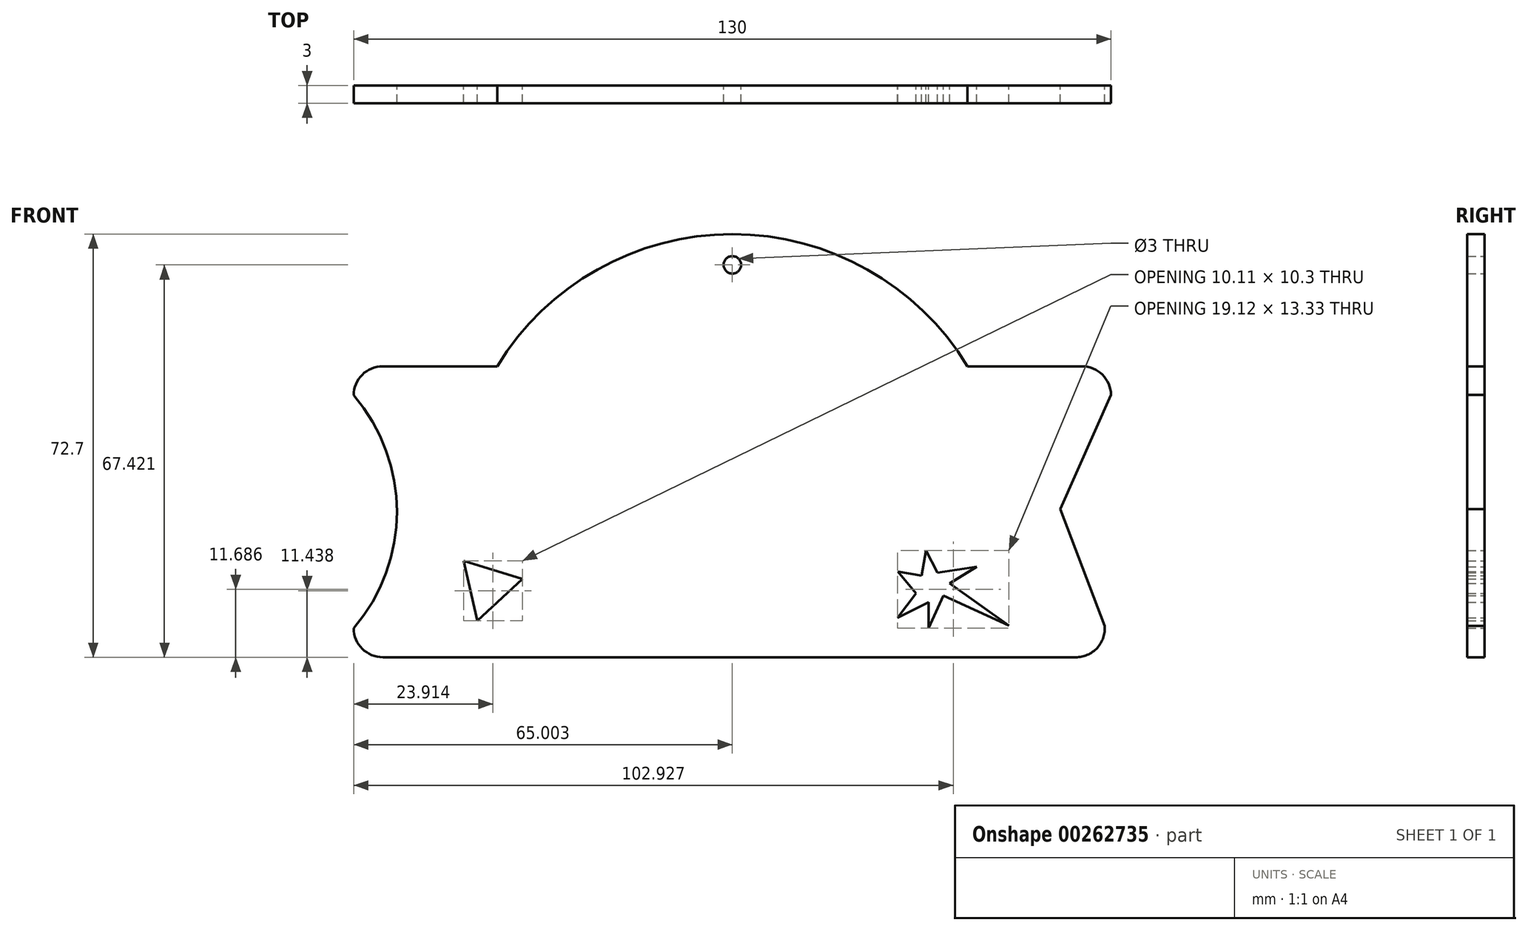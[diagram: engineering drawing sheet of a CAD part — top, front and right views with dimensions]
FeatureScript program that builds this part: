
annotation { "Feature Type Name" : "Feature", "Feature Type Description" : "" }
export const myFeature = defineFeature(function(context is Context, id is Id, definition is map)
    precondition{}
    {
        {
            var Q0;
            Q0=qCreatedBy(makeId("Front.planeOp"),FACE);
            var sketch = newSketch(context, id + "F0", { "sketchPlane" : qUnion([Q0])});
            skLineSegment(sketch, "E0.bottom", {"start": v(-100.37, 0) * mm, "end": v(18.58, 0) * mm});
            skLineSegment(sketch, "E0.top", {"start": v(-100.37, 50) * mm, "end": v(19.63, 50) * mm});
            skPoint(sketch, "E1", {"position": v(-40.37, 50) * mm});
            skPoint(sketch, "E2", {"position": v(15.96, 25.45) * mm});
            skArc(sketch, "E3", {"start": v(0, 50) * mm, "mid": v(-40.37, 72.7) * mm, "end": v(-80.73, 50) * mm});
            skCircle(sketch, "E4", {"center": v(-40.37, 67.42) * mm, "radius": 1.5 * mm});
            skPoint(sketch, "E5", {"position": v(-40.37, 39.6) * mm});
            skPoint(sketch, "E6", {"position": v(-105.37, 25) * mm});
            skPoint(sketch, "E7", {"position": v(-40.37, 0) * mm});
            skPoint(sketch, "E8", {"position": v(95.57, 25) * mm});
            skPoint(sketch, "E9.visualSharp", {"position": v(-105.37, 50) * mm});
            skArc(sketch, "E9.filletArc", {"start": v(-100.37, 50) * mm, "mid": v(-103.9, 48.54) * mm, "end": v(-105.37, 45) * mm});
            skPoint(sketch, "E10.visualSharp", {"position": v(-105.37, 0) * mm});
            skArc(sketch, "E10.filletArc", {"start": v(-105.37, 5) * mm, "mid": v(-103.9, 1.46) * mm, "end": v(-100.37, 0) * mm});
            skPoint(sketch, "E11.visualSharp", {"position": v(24.63, 0) * mm});
            skArc(sketch, "E11.filletArc", {"start": v(18.58, 0) * mm, "mid": v(22.25, 1.6) * mm, "end": v(23.56, 5.4) * mm});
            skPoint(sketch, "E12.visualSharp", {"position": v(24.63, 50) * mm});
            skArc(sketch, "E12.filletArc", {"start": v(24.63, 45.07) * mm, "mid": v(23.14, 48.56) * mm, "end": v(19.63, 50) * mm});
            skArc(sketch, "E13", {"start": v(-105.37, 5) * mm, "mid": v(-97.95, 25) * mm, "end": v(-105.37, 45) * mm});
            skLineSegment(sketch, "E14", {"start": v(24.63, 45.07) * mm, "end": v(15.96, 25.45) * mm});
            skLineSegment(sketch, "E15", {"start": v(15.96, 25.45) * mm, "end": v(23.56, 5.4) * mm});
            skLineSegment(sketch, "E16", {"start": v(-7.12, 18.35) * mm, "end": v(-7.86, 14.02) * mm});
            skLineSegment(sketch, "E17", {"start": v(-7.86, 14.02) * mm, "end": v(-11.97, 14.72) * mm});
            skLineSegment(sketch, "E18", {"start": v(-11.97, 14.72) * mm, "end": v(-8.83, 10.98) * mm});
            skLineSegment(sketch, "E19", {"start": v(-8.83, 10.98) * mm, "end": v(-12, 6.8) * mm});
            skLineSegment(sketch, "E20", {"start": v(-12, 6.8) * mm, "end": v(-6.68, 9.46) * mm});
            skLineSegment(sketch, "E21", {"start": v(-6.68, 9.46) * mm, "end": v(-6.68, 5.02) * mm});
            skLineSegment(sketch, "E22", {"start": v(-6.68, 5.02) * mm, "end": v(-4.14, 10.6) * mm});
            skLineSegment(sketch, "E23", {"start": v(-4.14, 10.6) * mm, "end": v(7.12, 5.48) * mm});
            skLineSegment(sketch, "E24", {"start": v(7.12, 5.48) * mm, "end": v(-3.07, 12.68) * mm});
            skLineSegment(sketch, "E25", {"start": v(-3.07, 12.68) * mm, "end": v(1.56, 15.54) * mm});
            skLineSegment(sketch, "E26", {"start": v(-7.12, 18.35) * mm, "end": v(-5.16, 14.53) * mm});
            skLineSegment(sketch, "E27", {"start": v(-5.16, 14.53) * mm, "end": v(1.56, 15.54) * mm});
            skCircle(sketch, "E28.cCircle", {"center": v(-82.35, 12.12) * mm, "radius": 3.05 * mm, "construction": true});
            skLineSegment(sketch, "E28.0", {"start": v(-86.5, 16.59) * mm, "end": v(-76.4, 13.49) * mm});
            skLineSegment(sketch, "E28.1", {"start": v(-76.4, 13.49) * mm, "end": v(-84.14, 6.29) * mm});
            skLineSegment(sketch, "E28.2", {"start": v(-84.14, 6.29) * mm, "end": v(-86.5, 16.59) * mm});
            skPoint(sketch, "E28.0.midPoint", {"position": v(-81.46, 15.04) * mm});
            skSolve(sketch);
        }
        {
            var Q0;
            Q0=makeQuery(id+"F0.imprint","IMPRINT",FACE,{"disambiguationData":[TD([[makeQuery(id+"F0.imprint","IMPRINT",EDGE,{"derivedFrom":sQuery(id+"F0.wireOp",EDGE,"E0.bottom")}),1.0]])]});
            var Q1;
            {var subQ0=sQuery(id+"F0.wireOp",EDGE,"E3");Q1=makeQuery(id+"F0.imprint","IMPRINT",FACE,{"disambiguationData":[TD([[makeQuery(id+"F0.imprint","IMPRINT",EDGE,{"derivedFrom":subQ0}),1.0]])]});}
            extrude(context, id + "F1", {"entities" : qUnion([Q0, Q1]), "depth" : 3 * mm});
        }
    });
